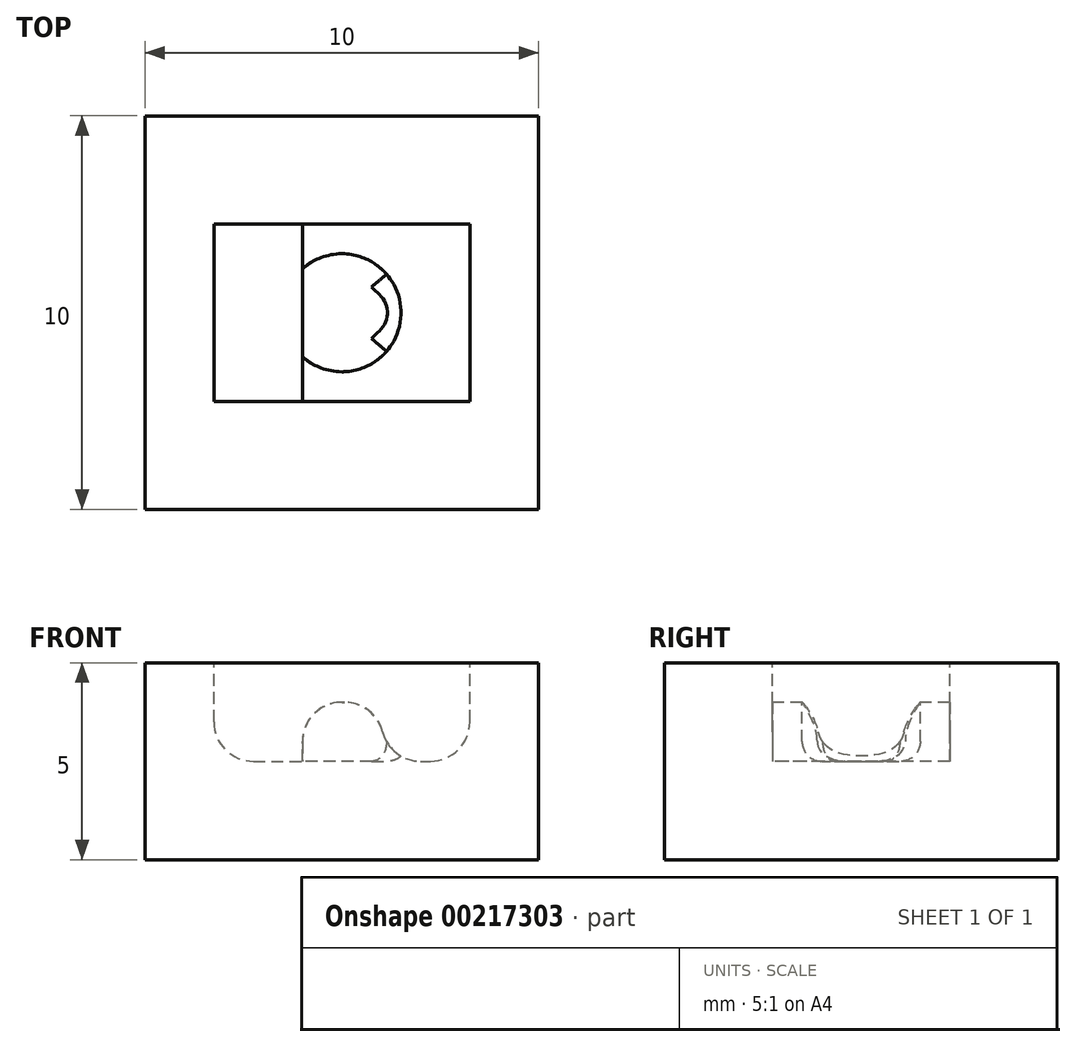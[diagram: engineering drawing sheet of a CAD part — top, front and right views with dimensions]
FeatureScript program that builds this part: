
annotation { "Feature Type Name" : "Feature", "Feature Type Description" : "" }
export const myFeature = defineFeature(function(context is Context, id is Id, definition is map)
    precondition{}
    {
        {
            var Q0;
            Q0=qCreatedBy(makeId("Top.planeOp"),FACE);
            var sketch = newSketch(context, id + "F0", { "sketchPlane" : qUnion([Q0])});
            skLineSegment(sketch, "E0.bottom", {"start": v(-7.58, 3.27) * mm, "end": v(2.42, 3.27) * mm});
            skLineSegment(sketch, "E0.top", {"start": v(-7.58, -6.73) * mm, "end": v(2.42, -6.73) * mm});
            skLineSegment(sketch, "E0.left", {"start": v(-7.58, 3.27) * mm, "end": v(-7.58, -6.73) * mm});
            skLineSegment(sketch, "E0.right", {"start": v(2.42, 3.27) * mm, "end": v(2.42, -6.73) * mm});
            skSolve(sketch);
        }
        {
            var Q0;
            Q0=makeQuery(id+"F0.imprint","IMPRINT",FACE,{"disambiguationData":[TD([[makeQuery(id+"F0.imprint","IMPRINT",EDGE,{"derivedFrom":sQuery(id+"F0.wireOp",EDGE,"E0.bottom")}),-1.0]])]});
            extrude(context, id + "F1", {"entities" : qUnion([Q0]), "depth" : 5 * mm});
        }
        {
            var Q0;
            Q0=makeQuery(id+"F1.opExtrude","CAP_FACE",FACE,{"disambiguationData":[OSD([sQuery(id+"F0.wireOp",EDGE,"E0.bottom"),sQuery(id+"F0.wireOp",EDGE,"E0.top"),sQuery(id+"F0.wireOp",EDGE,"E0.left"),sQuery(id+"F0.wireOp",EDGE,"E0.right")])],"isStart":false});
            var sketch = newSketch(context, id + "F2", { "sketchPlane" : qUnion([Q0])});
            skLineSegment(sketch, "E1.bottom", {"start": v(-5.83, 0.52) * mm, "end": v(0.67, 0.52) * mm});
            skLineSegment(sketch, "E1.top", {"start": v(-5.83, -3.98) * mm, "end": v(0.67, -3.98) * mm});
            skLineSegment(sketch, "E1.left", {"start": v(-5.83, 0.52) * mm, "end": v(-5.83, -3.98) * mm});
            skLineSegment(sketch, "E1.right", {"start": v(0.67, 0.52) * mm, "end": v(0.67, -3.98) * mm});
            skSolve(sketch);
        }
        {
            var Q0;
            Q0=makeQuery(id+"F2.imprint","IMPRINT",FACE,{"disambiguationData":[TD([[makeQuery(id+"F2.imprint","IMPRINT",EDGE,{"derivedFrom":sQuery(id+"F2.wireOp",EDGE,"E1.bottom")}),-1.0]])]});
            extrude(context, id + "F3", {"entities" : qUnion([Q0]), "operationType" : NewBodyOperationType.REMOVE, "oppositeDirection" : true, "depth" : 2.5 * mm});
        }
        {
            var Q0;
            Q0=makeQuery(id+"F3.boolean.opBoolean","COPY",FACE,{"derivedFrom":makeQuery(id+"F3.opExtrude","CAP_FACE",FACE,{"disambiguationData":[OSD([sQuery(id+"F2.wireOp",EDGE,"E1.bottom"),sQuery(id+"F2.wireOp",EDGE,"E1.top"),sQuery(id+"F2.wireOp",EDGE,"E1.left"),sQuery(id+"F2.wireOp",EDGE,"E1.right")])],"isStart":false})});
            var sketch = newSketch(context, id + "F4", { "sketchPlane" : qUnion([Q0])});
            skLineSegment(sketch, "E2.bottom", {"start": v(-3.58, 0.52) * mm, "end": v(-1.58, 0.52) * mm});
            skLineSegment(sketch, "E2.top", {"start": v(-3.58, -3.98) * mm, "end": v(-1.58, -3.98) * mm});
            skLineSegment(sketch, "E2.left", {"start": v(-3.58, 0.52) * mm, "end": v(-3.58, -3.98) * mm});
            skLineSegment(sketch, "E2.right", {"start": v(-1.58, 0.52) * mm, "end": v(-1.58, -3.98) * mm});
            skSolve(sketch);
        }
        {
            var Q0;
            Q0=makeQuery(id+"F4.imprint","IMPRINT",FACE,{"disambiguationData":[TD([[makeQuery(id+"F4.imprint","IMPRINT",EDGE,{"derivedFrom":sQuery(id+"F4.wireOp",EDGE,"E2.bottom")}),-1.0]])]});
            extrude(context, id + "F5", {"entities" : qUnion([Q0]), "operationType" : NewBodyOperationType.ADD, "depth" : 1.5 * mm});
        }
        {
            var Q0;
            Q0=makeQuery(id+"F3.boolean.opBoolean","COPY",EDGE,{"derivedFrom":makeQuery(id+"F3.opExtrude","CAP_EDGE",EDGE,{"disambiguationData":[OSD([sQuery(id+"F2.wireOp",EDGE,"E1.left")])],"isStart":false})});
            var Q1;
            Q1=makeQuery(id+"F3.boolean.opBoolean","COPY",EDGE,{"derivedFrom":makeQuery(id+"F3.opExtrude","CAP_EDGE",EDGE,{"disambiguationData":[OSD([sQuery(id+"F2.wireOp",EDGE,"E1.right")])],"isStart":false})});
            var Q2;
            Q2=makeQuery(id+"F5.opExtrude","CAP_EDGE",EDGE,{"disambiguationData":[OSD([sQuery(id+"F4.wireOp",EDGE,"E2.left")])],"isStart":true});
            var Q3;
            Q3=makeQuery(id+"F5.opExtrude","CAP_EDGE",EDGE,{"disambiguationData":[OSD([sQuery(id+"F4.wireOp",EDGE,"E2.right")])],"isStart":true});
            fillet(context, id + "F6", {"entities" : qUnion([Q0, Q1, Q2, Q3]), "radius" : 1 * mm, "tangentPropagation" : true, "allowEdgeOverflow" : false});
        }
        {
            var Q0;
            Q0=makeQuery(id+"F5.opExtrude","CAP_EDGE",EDGE,{"disambiguationData":[OSD([sQuery(id+"F4.wireOp",EDGE,"E2.left")])],"isStart":false});
            var Q1;
            Q1=makeQuery(id+"F5.opExtrude","CAP_EDGE",EDGE,{"disambiguationData":[OSD([sQuery(id+"F4.wireOp",EDGE,"E2.right")])],"isStart":false});
            fillet(context, id + "F7", {"entities" : qUnion([Q0, Q1]), "radius" : 1 * mm, "tangentPropagation" : true, "allowEdgeOverflow" : false});
        }
        {
            var Q0;
            Q0=makeQuery(id+"F1.opExtrude","CAP_FACE",FACE,{"disambiguationData":[OSD([sQuery(id+"F0.wireOp",EDGE,"E0.bottom"),sQuery(id+"F0.wireOp",EDGE,"E0.top"),sQuery(id+"F0.wireOp",EDGE,"E0.left"),sQuery(id+"F0.wireOp",EDGE,"E0.right")])],"isStart":false});
            var sketch = newSketch(context, id + "F8", { "sketchPlane" : qUnion([Q0])});
            skCircle(sketch, "E3", {"center": v(-2.58, -1.73) * mm, "radius": 1.5 * mm});
            skSolve(sketch);
        }
        {
            var Q0;
            Q0 = qSketchRegion(id + "F8", true);
            extrude(context, id + "F9", {"entities" : qUnion([Q0]), "operationType" : NewBodyOperationType.REMOVE, "oppositeDirection" : true, "depth" : 2.5 * mm});
        }
        {
            var Q0;
            Q0=makeQuery(id+"F9.boolean.opBoolean","COPY",EDGE,{"derivedFrom":makeQuery(id+"F9.opExtrude","CAP_EDGE",EDGE,{"disambiguationData":[OSD([sQuery(id+"F8.wireOp",EDGE,"E3")])],"isStart":false})});
            fillet(context, id + "F10", {"entities" : qUnion([Q0]), "radius" : 0.5 * mm, "tangentPropagation" : true, "allowEdgeOverflow" : false});
        }
    });
